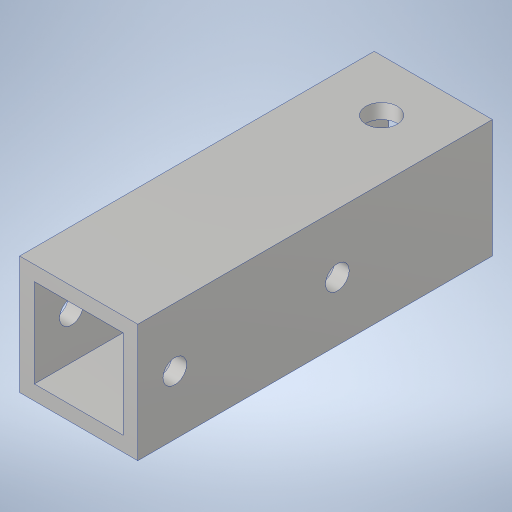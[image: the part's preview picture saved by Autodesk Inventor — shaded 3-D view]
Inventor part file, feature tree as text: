
AUTODESK INVENTOR PART (.ipt)
format: ipt  version: 2023.4 (Build 274418000, 418)  size: 224,256 bytes
history: native  units: in
note: dims shown in document units (in); Inventor stores cm internally (conversion verified against a paired STEP export)
features: hole x2, sketch x2, extrude x1
ambient origin geometry x8: Origin, YZ Plane, XZ Plane, XY Plane, X Axis, Y Axis, Z Axis, Center Point
bodies: Solid1 (feature_tree)
feature tree (5):
  extrude  "Extrusion1"  Depth=1.375in
  hole  "Hole2"  [1 undecoded]
  hole  "Hole3"  [1 undecoded]
  sketch  "Sketch3"  dims[d4=0.0in d22=1.375in]
  sketch  "Sketch4"  dims[d23=0.201in d24=0.75in d25=0.385in d26=0.25in d27=0.5635in d28=1.0in d29=0.8108in d30=0.266in d31=0.75in d32=0.762in d33=0.25in d34=0.5635in d35=1.0in d36=0.8108in d37=0.313in d38=0.4375in]
note: 2 required parameter values undecoded (feature->parameter linkage not recoverable at this tier; creation-order binding heuristic only, values carry confidence <= 0.55)
